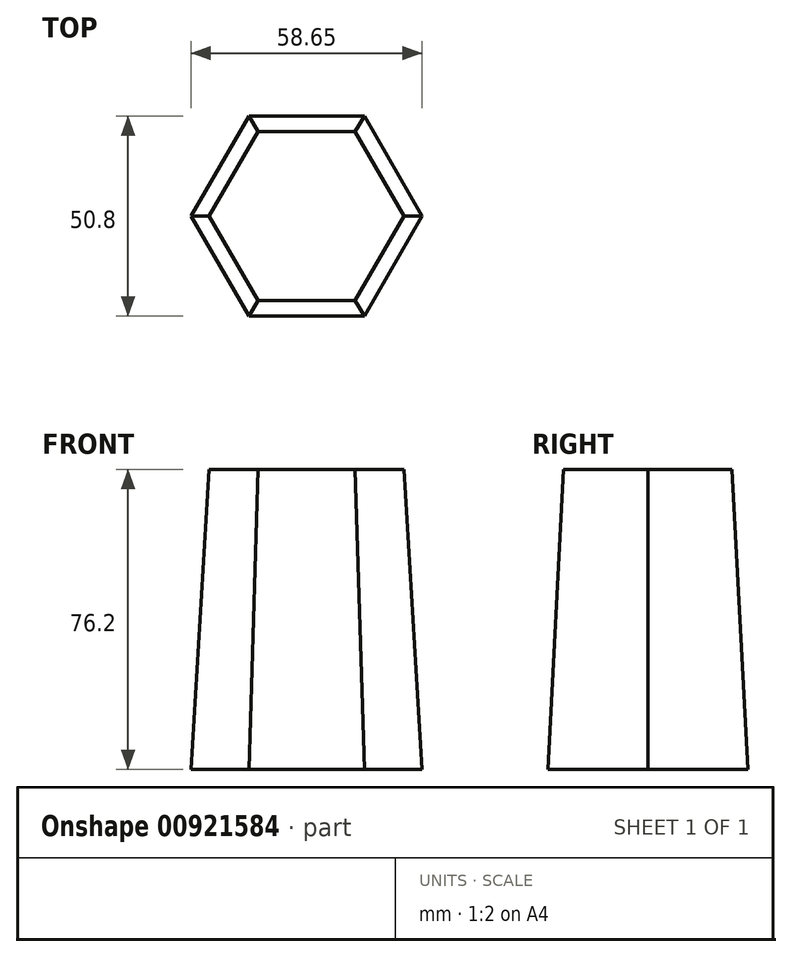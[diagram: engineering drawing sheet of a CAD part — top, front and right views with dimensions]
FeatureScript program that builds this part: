
annotation { "Feature Type Name" : "Feature", "Feature Type Description" : "" }
export const myFeature = defineFeature(function(context is Context, id is Id, definition is map)
    precondition{}
    {
        {
            var Q0;
            Q0=qCreatedBy(makeId("Top.planeOp"),FACE);
            var sketch = newSketch(context, id + "F0", { "sketchPlane" : qUnion([Q0])});
            skCircle(sketch, "E0.cCircle", {"center": v(-14.66, 25.4) * mm, "radius": 25.4 * mm, "construction": true});
            skLineSegment(sketch, "E0.0", {"start": v(-29.33, 0) * mm, "end": v(-44, 25.4) * mm});
            skLineSegment(sketch, "E0.1", {"start": v(-44, 25.4) * mm, "end": v(-29.33, 50.8) * mm});
            skLineSegment(sketch, "E0.2", {"start": v(-29.33, 50.8) * mm, "end": v(0, 50.8) * mm});
            skLineSegment(sketch, "E0.3", {"start": v(0, 50.8) * mm, "end": v(14.66, 25.4) * mm});
            skLineSegment(sketch, "E0.4", {"start": v(14.66, 25.4) * mm, "end": v(0, 0) * mm});
            skLineSegment(sketch, "E0.5", {"start": v(0, 0) * mm, "end": v(-29.33, 0) * mm});
            skPoint(sketch, "E0.0.midPoint", {"position": v(-36.66, 12.7) * mm});
            skSolve(sketch);
        }
        {
            var Q0;
            Q0=makeQuery(id+"F0.imprint","IMPRINT",FACE,{"disambiguationData":[TD([[makeQuery(id+"F0.imprint","IMPRINT",EDGE,{"derivedFrom":sQuery(id+"F0.wireOp",EDGE,"E0.0")}),-1.0]])]});
            extrude(context, id + "F1", {"entities" : qUnion([Q0]), "depth" : 76.2 * mm, "offsetDistance" : 25.4 * mm, "hasDraft" : true, "draftAngle" : 3 * degree, "draftPullDirection" : true});
        }
    });
